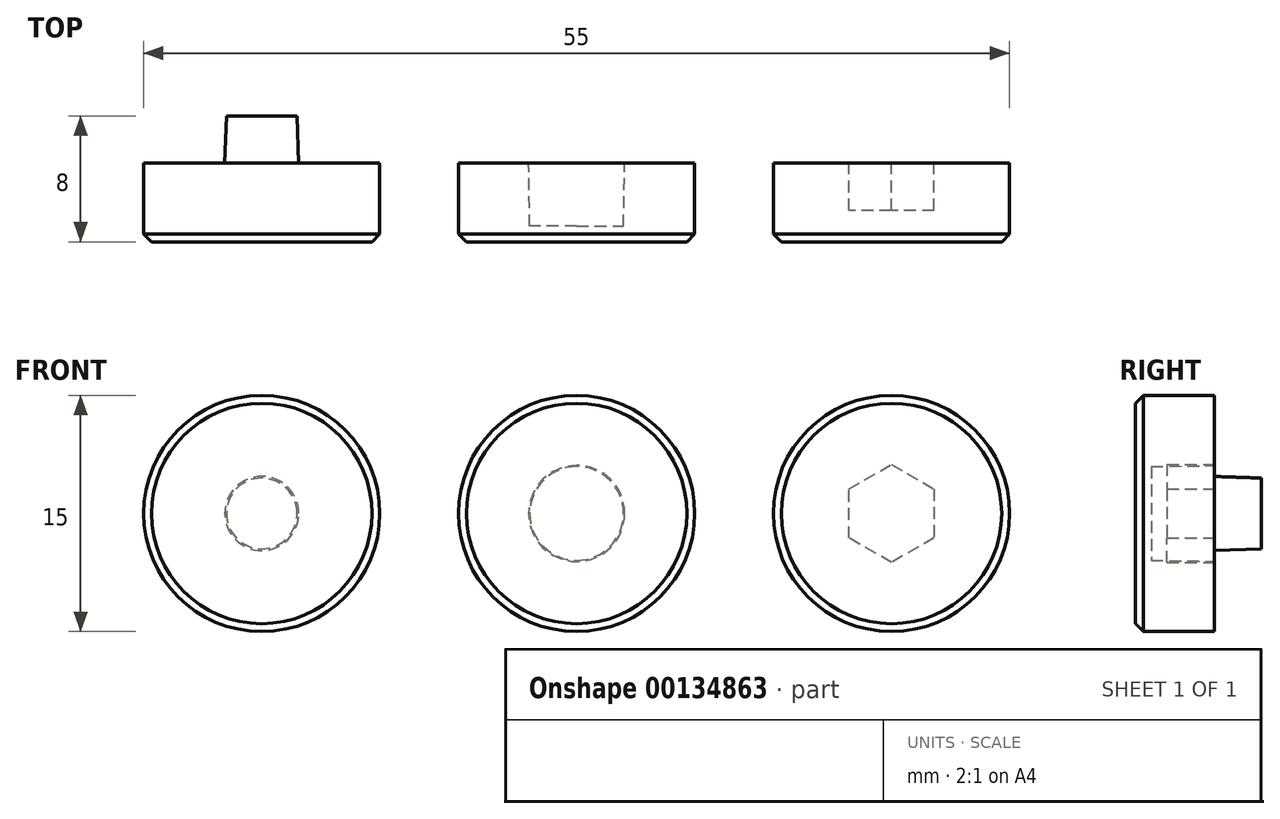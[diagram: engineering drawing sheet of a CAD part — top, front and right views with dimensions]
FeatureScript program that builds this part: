
annotation { "Feature Type Name" : "Feature", "Feature Type Description" : "" }
export const myFeature = defineFeature(function(context is Context, id is Id, definition is map)
    precondition{}
    {
        {
            var Q0;
            Q0=qCreatedBy(makeId("Front.planeOp"),FACE);
            var sketch = newSketch(context, id + "F0", { "sketchPlane" : qUnion([Q0])});
            skCircle(sketch, "E0", {"center": v(0, 0) * mm, "radius": 7.5 * mm});
            skSolve(sketch);
        }
        {
            var Q0;
            Q0=qSketchRegion(id+"F0",true);
            extrude(context, id + "F1", {"entities" : qUnion([Q0]), "depth" : 5 * mm});
        }
        {
            var Q0;
            Q0=makeQuery(id+"F1.opExtrude","CAP_FACE",FACE,{"disambiguationData":[OSD([sQuery(id+"F0.wireOp",EDGE,"E0")])],"isStart":true});
            var sketch = newSketch(context, id + "F2", { "sketchPlane" : qUnion([Q0])});
            skCircle(sketch, "E1", {"center": v(0, 0) * mm, "radius": 2.35 * mm});
            skSolve(sketch);
        }
        {
            var Q0;
            Q0=qSketchRegion(id+"F2",true);
            extrude(context, id + "F3", {"entities" : qUnion([Q0]), "operationType" : NewBodyOperationType.ADD, "depth" : 3 * mm, "hasDraft" : true, "draftAngle" : 2 * degree, "draftPullDirection" : true});
        }
        {
            var Q0;
            Q0=makeQuery(id+"F1.opExtrude","CAP_EDGE",EDGE,{"disambiguationData":[OSD([sQuery(id+"F0.wireOp",EDGE,"E0")])],"isStart":false});
            chamfer(context, id + "F4", {"entities" : qUnion([Q0]), "width" : 0.5 * mm, "tangentPropagation" : true});
        }
        {
            var Q0;
            Q0=makeQuery(id+"F1.opExtrude","SWEPT_BODY",BODY,{"disambiguationData":[OSD([sQuery(id+"F0.wireOp",EDGE,"E0")])]});
            transform(context, id + "F5", {"entities" : qUnion([Q0]), "transformType" : TransformType.TRANSLATION_3D, "dx" : 20 * mm, "dy" : 0 * mm, "dz" : 0 * mm, "makeCopy" : true});
        }
        {
            var Q0;
            Q0=makeQuery(id+"F5.opPattern","COPY",FACE,{"derivedFrom":makeQuery(id+"F3.opExtrude","CAP_FACE",FACE,{"disambiguationData":[OSD([sQuery(id+"F2.wireOp",EDGE,"E1")])],"isStart":false}),"instanceName":"1"});
            var sketch = newSketch(context, id + "F6", { "sketchPlane" : qUnion([Q0])});
            skCircle(sketch, "E2", {"center": v(-20, 0) * mm, "radius": 3.1 * mm});
            skSolve(sketch);
        }
        {
            var Q0;
            Q0=qSketchRegion(id+"F6",true);
            extrude(context, id + "F7", {"entities" : qUnion([Q0]), "operationType" : NewBodyOperationType.REMOVE, "oppositeDirection" : true, "depth" : 7 * mm, "hasDraft" : true, "draftAngle" : 1 * degree, "draftPullDirection" : true});
        }
        {
            var Q0;
            Q0=makeQuery(id+"F1.opExtrude","SWEPT_BODY",BODY,{"disambiguationData":[OSD([sQuery(id+"F0.wireOp",EDGE,"E0")])]});
            transform(context, id + "F8", {"entities" : qUnion([Q0]), "transformType" : TransformType.TRANSLATION_3D, "dx" : 40 * mm, "dy" : 0 * mm, "dz" : 0 * mm, "makeCopy" : true});
        }
        {
            var Q0;
            Q0=makeQuery(id+"F8.opPattern","COPY",FACE,{"derivedFrom":makeQuery(id+"F3.opExtrude","CAP_FACE",FACE,{"disambiguationData":[OSD([sQuery(id+"F2.wireOp",EDGE,"E1")])],"isStart":false}),"instanceName":"1"});
            var sketch = newSketch(context, id + "F9", { "sketchPlane" : qUnion([Q0])});
            skCircle(sketch, "E3.cCircle", {"center": v(-40, 0) * mm, "radius": 2.7 * mm, "construction": true});
            skLineSegment(sketch, "E3.0", {"start": v(-37.3, 1.56) * mm, "end": v(-37.3, -1.56) * mm});
            skLineSegment(sketch, "E3.1", {"start": v(-37.3, -1.56) * mm, "end": v(-40, -3.12) * mm});
            skLineSegment(sketch, "E3.2", {"start": v(-40, -3.12) * mm, "end": v(-42.7, -1.56) * mm});
            skLineSegment(sketch, "E3.3", {"start": v(-42.7, -1.56) * mm, "end": v(-42.7, 1.56) * mm});
            skLineSegment(sketch, "E3.4", {"start": v(-42.7, 1.56) * mm, "end": v(-40, 3.12) * mm});
            skLineSegment(sketch, "E3.5", {"start": v(-40, 3.12) * mm, "end": v(-37.3, 1.56) * mm});
            skPoint(sketch, "E3.0.midPoint", {"position": v(-37.3, 0) * mm});
            skSolve(sketch);
        }
        {
            var Q0;
            Q0=qSketchRegion(id+"F9",true);
            extrude(context, id + "F10", {"entities" : qUnion([Q0]), "operationType" : NewBodyOperationType.REMOVE, "oppositeDirection" : true, "depth" : 6 * mm});
        }
    });
